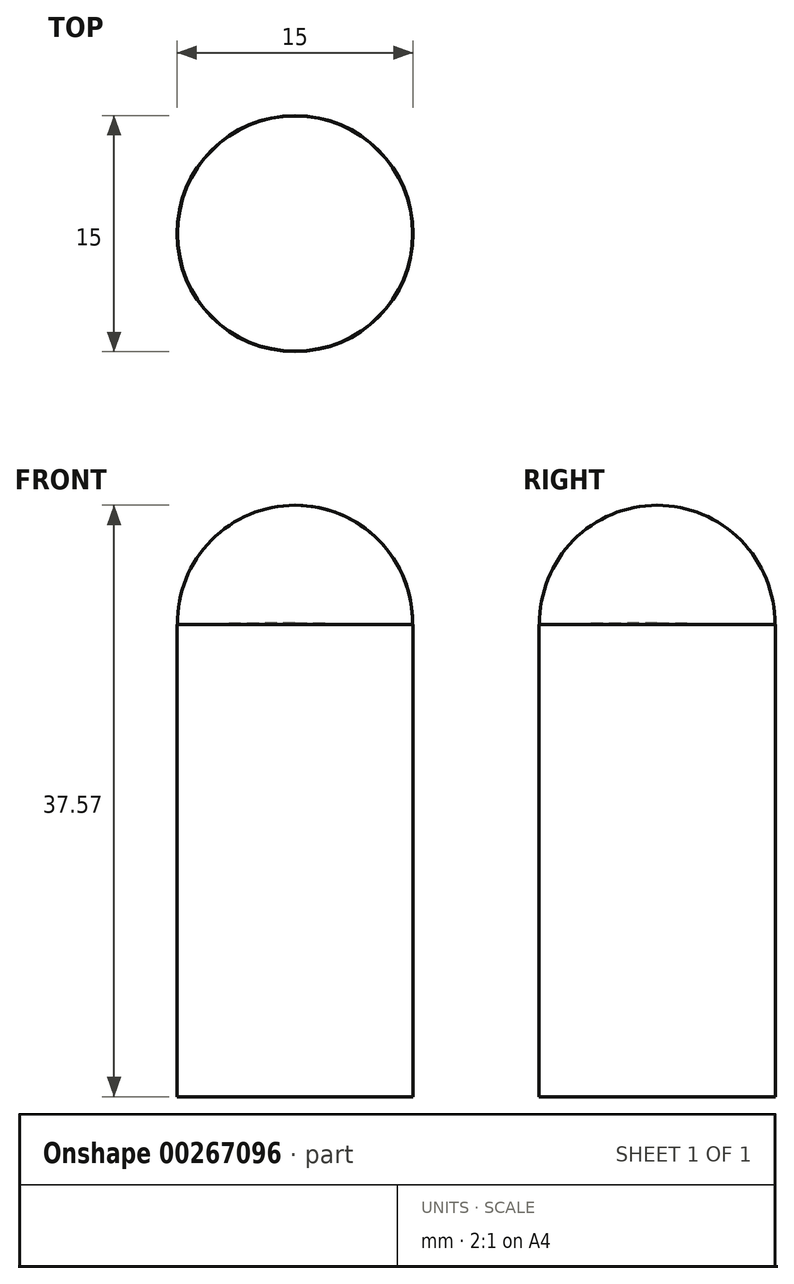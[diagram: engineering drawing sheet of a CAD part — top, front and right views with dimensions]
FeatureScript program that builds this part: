
annotation { "Feature Type Name" : "Feature", "Feature Type Description" : "" }
export const myFeature = defineFeature(function(context is Context, id is Id, definition is map)
    precondition{}
    {
        {
            var Q0;
            Q0=qCreatedBy(makeId("Top.planeOp"),FACE);
            var sketch = newSketch(context, id + "F0", { "sketchPlane" : qUnion([Q0])});
            skCircle(sketch, "E0", {"center": v(0, 0) * mm, "radius": 7.5 * mm});
            skSolve(sketch);
        }
        {
            var Q0;
            Q0=makeQuery(id+"F0.imprint","IMPRINT",FACE,{"disambiguationData":[TD([[makeQuery(id+"F0.imprint","IMPRINT",EDGE,{"derivedFrom":sQuery(id+"F0.wireOp",EDGE,"E0")}),1.0]])]});
            extrude(context, id + "F1", {"entities" : qUnion([Q0]), "depth" : 30 * mm});
        }
        {
            var Q0;
            Q0=qCreatedBy(makeId("Front.planeOp"),FACE);
            var sketch = newSketch(context, id + "F2", { "sketchPlane" : qUnion([Q0])});
            skArc(sketch, "E1", {"start": v(7.47, 30) * mm, "mid": v(5.32, 35.34) * mm, "end": v(0, 37.57) * mm});
            skLineSegment(sketch, "E2", {"start": v(0, 30.1) * mm, "end": v(0, 37.57) * mm});
            skLineSegment(sketch, "E3", {"start": v(0, 30.1) * mm, "end": v(7.47, 30) * mm});
            skSolve(sketch);
        }
        {
            var Q0;
            Q0=makeQuery(id+"F2.imprint","IMPRINT",FACE,{"disambiguationData":[TD([[makeQuery(id+"F2.imprint","IMPRINT",EDGE,{"derivedFrom":sQuery(id+"F2.wireOp",EDGE,"E1")}),1.0]])]});
            var Q1;
            Q1=sQuery(id+"F2.wireOp",EDGE,"E2");
            revolve(context, id + "F3", {"entities" : qUnion([Q0]), "axis" : qUnion([Q1]), "revolveType" : RevolveType.FULL});
        }
    });
